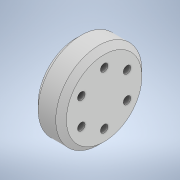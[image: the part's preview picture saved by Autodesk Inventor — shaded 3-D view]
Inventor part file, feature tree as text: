
AUTODESK INVENTOR PART (.ipt)
format: ipt  version: 2022 (Build 260153000, 153)  size: 174,592 bytes
history: native  units: mm
features: sketch x4, revolve x2, hole x2, other x1
ambient origin geometry x8: Origin, YZ Plane, XZ Plane, XY Plane, X Axis, Y Axis, Z Axis, Center Point
bodies: Body1 (feature_tree)
feature tree (9):
  other  "Твердое тело1"
  revolve  "Вращение1"
  revolve  "Вращение2"
  hole  "Отверстие1"  [1 undecoded]
  hole  "Отверстие2"  [1 undecoded]
  sketch  "Эскиз1"
  sketch  "Эскиз2"
  sketch  "Эскиз3"
  sketch  "Эскиз4"
note: 2 required parameter values undecoded (feature->parameter linkage not recoverable at this tier; creation-order binding heuristic only, values carry confidence <= 0.55)
